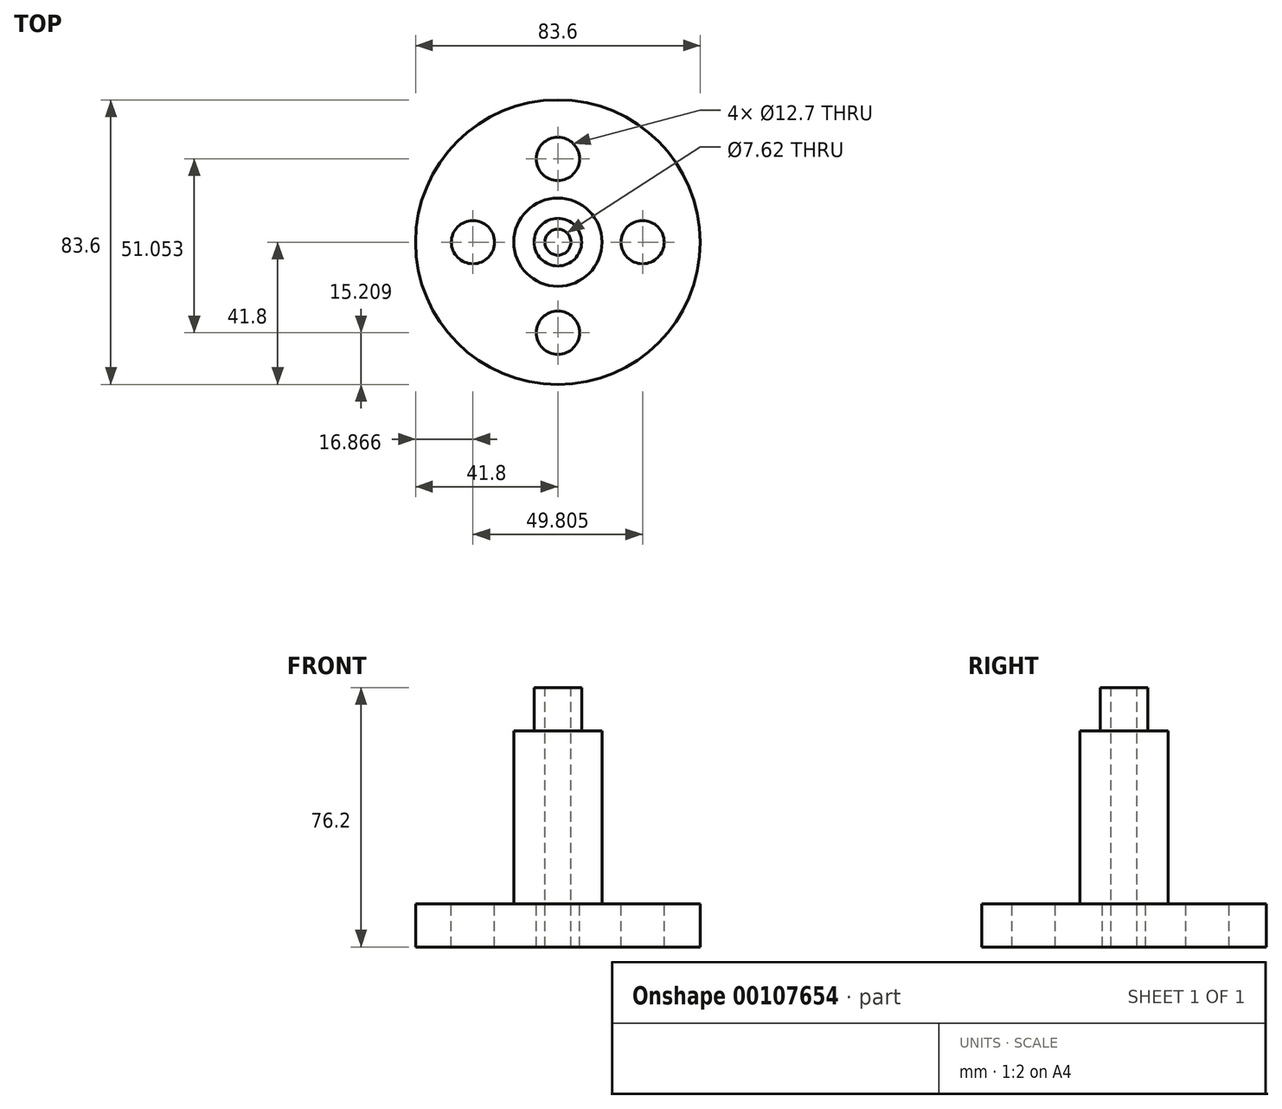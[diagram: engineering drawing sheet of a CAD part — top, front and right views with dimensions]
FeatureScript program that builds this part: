
annotation { "Feature Type Name" : "Feature", "Feature Type Description" : "" }
export const myFeature = defineFeature(function(context is Context, id is Id, definition is map)
    precondition{}
    {
        {
            var Q0;
            Q0=qCreatedBy(makeId("Top.planeOp"),FACE);
            var sketch = newSketch(context, id + "F0", { "sketchPlane" : qUnion([Q0])});
            skCircle(sketch, "E0", {"center": v(0, 0) * mm, "radius": 41.8 * mm});
            skSolve(sketch);
        }
        {
            var Q0;
            Q0=makeQuery(id+"F0.imprint","IMPRINT",FACE,{"disambiguationData":[TD([[makeQuery(id+"F0.imprint","IMPRINT",EDGE,{"derivedFrom":sQuery(id+"F0.wireOp",EDGE,"E0")}),1.0]])]});
            extrude(context, id + "F1", {"entities" : qUnion([Q0]), "depth" : 12.7 * mm});
        }
        {
            var Q0;
            Q0=makeQuery(id+"F1.opExtrude","CAP_FACE",FACE,{"disambiguationData":[OSD([sQuery(id+"F0.wireOp",EDGE,"E0")])],"isStart":false});
            var sketch = newSketch(context, id + "F2", { "sketchPlane" : qUnion([Q0])});
            skCircle(sketch, "E1", {"center": v(0, 0) * mm, "radius": 12.96 * mm});
            skSolve(sketch);
        }
        {
            var Q0;
            Q0 = qSketchRegion(id + "F2", true);
            extrude(context, id + "F3", {"entities" : qUnion([Q0]), "operationType" : NewBodyOperationType.ADD, "depth" : 50.8 * mm});
        }
        {
            var Q0;
            Q0=makeQuery(id+"F3.opExtrude","CAP_FACE",FACE,{"disambiguationData":[OSD([sQuery(id+"F2.wireOp",EDGE,"E1")])],"isStart":false});
            var sketch = newSketch(context, id + "F4", { "sketchPlane" : qUnion([Q0])});
            skCircle(sketch, "E2", {"center": v(0, 0) * mm, "radius": 6.98 * mm});
            skSolve(sketch);
        }
        {
            var Q0;
            Q0 = qSketchRegion(id + "F4", true);
            var Q1;
            Q1=makeQuery(id+"F4.imprint","IMPRINT",FACE,{"disambiguationData":[TD([[makeQuery(id+"F4.imprint","IMPRINT",EDGE,{"derivedFrom":sQuery(id+"F4.wireOp",EDGE,"E2")}),1.0]])]});
            extrude(context, id + "F5", {"entities" : qUnion([Q0, Q1]), "operationType" : NewBodyOperationType.ADD, "depth" : 12.7 * mm});
        }
        {
            var Q0;
            Q0=makeQuery(id+"F5.opExtrude","CAP_FACE",FACE,{"disambiguationData":[OSD([sQuery(id+"F4.wireOp",EDGE,"E2")])],"isStart":false});
            var sketch = newSketch(context, id + "F6", { "sketchPlane" : qUnion([Q0])});
            skCircle(sketch, "E3", {"center": v(0, 0) * mm, "radius": 4.14 * mm});
            skSolve(sketch);
        }
        {
            var Q0;
            Q0=makeQuery(id+"F6.imprint","IMPRINT",FACE,{"disambiguationData":[TD([[makeQuery(id+"F6.imprint","IMPRINT",EDGE,{"derivedFrom":sQuery(id+"F6.wireOp",EDGE,"E3")}),1.0]])]});
            var sketch = newSketch(context, id + "F7", { "sketchPlane" : qUnion([Q0])});
            skPoint(sketch, "E4", {"position": v(0, 0) * mm});
            skSolve(sketch);
        }
        {
            var Q0;
            Q0=sQuery(id+"F7.wireOp",VERTEX,"E4");
            var Q1;
            Q1=makeQuery(id+"F1.opExtrude","SWEPT_BODY",BODY,{"disambiguationData":[OSD([sQuery(id+"F0.wireOp",EDGE,"E0")])]});
            hole(context, id + "F8", {"style" : HoleStyle.SIMPLE, "endStyle" : HoleEndStyle.THROUGH, "holeDiameter" : 7.62 * mm, "locations" : qUnion([Q0]), "scope" : qUnion([Q1]), "isTappedThrough" : true});
        }
        {
            var Q0;
            Q0=makeQuery(id+"F1.opExtrude","CAP_FACE",FACE,{"disambiguationData":[OSD([sQuery(id+"F0.wireOp",EDGE,"E0")])],"isStart":false});
            var sketch = newSketch(context, id + "F9", { "sketchPlane" : qUnion([Q0])});
            skPoint(sketch, "E5", {"position": v(0, -26.6) * mm});
            skPoint(sketch, "E6", {"position": v(24.87, 0) * mm});
            skPoint(sketch, "E7", {"position": v(0, 24.46) * mm});
            skPoint(sketch, "E8", {"position": v(-24.93, 0) * mm});
            skSolve(sketch);
        }
        {
            var Q0;
            Q0=sQuery(id+"F9.wireOp",VERTEX,"E5");
            var Q1;
            Q1=sQuery(id+"F9.wireOp",VERTEX,"E8");
            var Q2;
            Q2=sQuery(id+"F9.wireOp",VERTEX,"E6");
            var Q3;
            Q3=sQuery(id+"F9.wireOp",VERTEX,"E7");
            var Q4;
            Q4=makeQuery(id+"F1.opExtrude","SWEPT_BODY",BODY,{"disambiguationData":[OSD([sQuery(id+"F0.wireOp",EDGE,"E0")])]});
            hole(context, id + "F10", {"style" : HoleStyle.SIMPLE, "endStyle" : HoleEndStyle.THROUGH, "holeDiameter" : 12.7 * mm, "locations" : qUnion([Q0, Q1, Q2, Q3]), "scope" : qUnion([Q4]), "isTappedThrough" : true});
        }
    });
